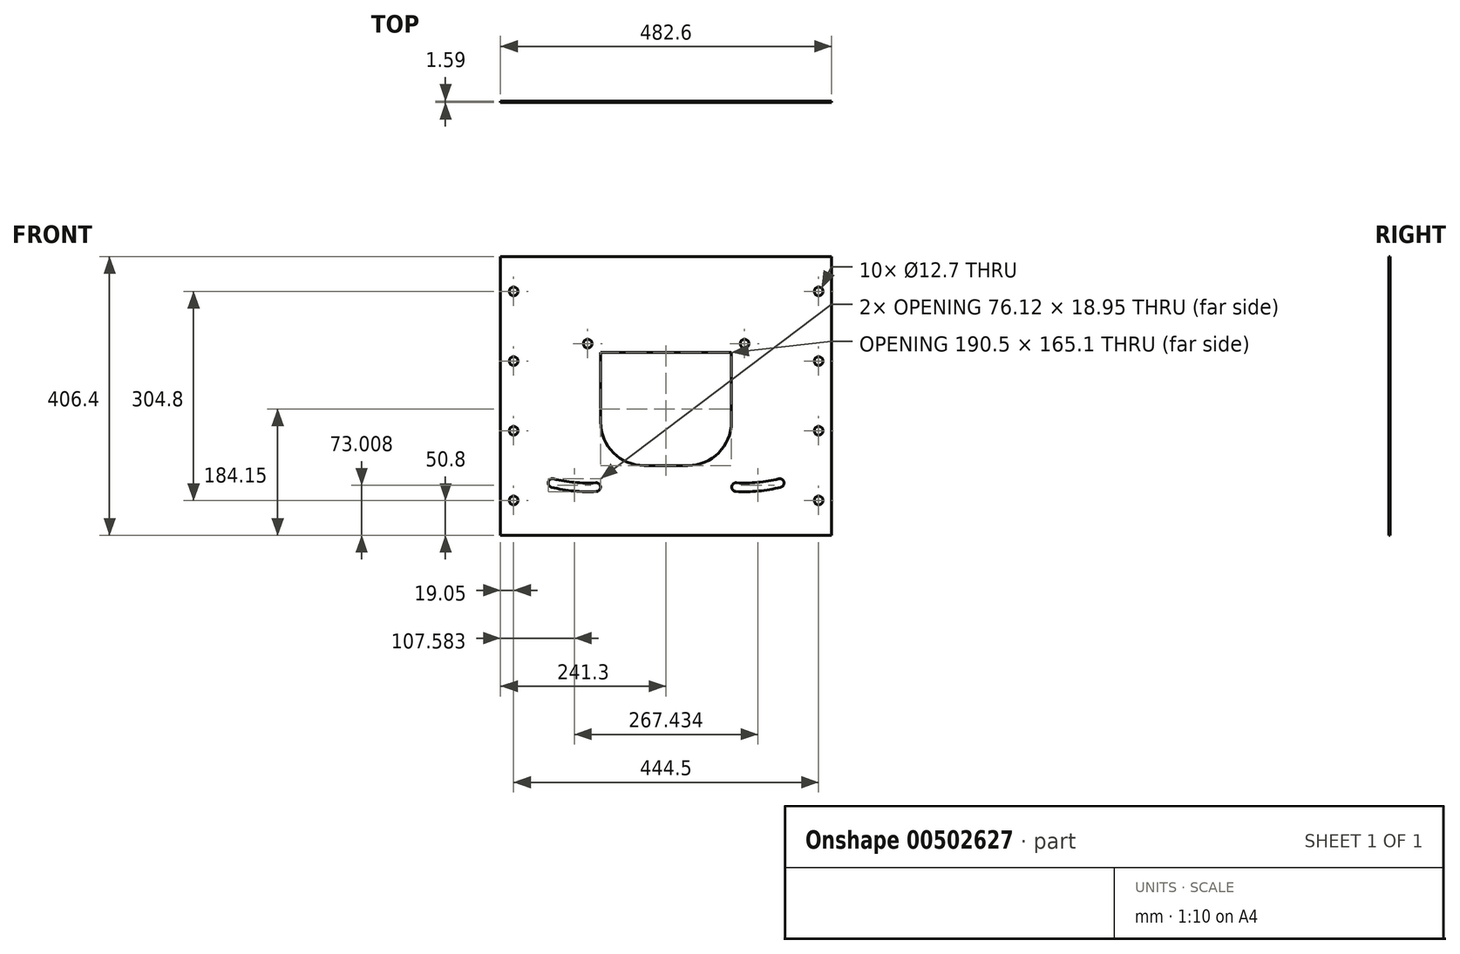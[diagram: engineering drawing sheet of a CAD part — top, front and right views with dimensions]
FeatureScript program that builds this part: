
annotation { "Feature Type Name" : "Feature", "Feature Type Description" : "" }
export const myFeature = defineFeature(function(context is Context, id is Id, definition is map)
    precondition{}
    {
        {
            var Q0;
            Q0=qCreatedBy(makeId("Front.planeOp"),FACE);
            var sketch = newSketch(context, id + "F0", { "sketchPlane" : qUnion([Q0])});
            skLineSegment(sketch, "E0.bottom", {"start": v(0, 0) * mm, "end": v(482.6, 0) * mm});
            skLineSegment(sketch, "E0.top", {"start": v(0, 304.8) * mm, "end": v(146.05, 304.8) * mm});
            skLineSegment(sketch, "E0.left", {"start": v(0, 0) * mm, "end": v(0, 304.8) * mm});
            skLineSegment(sketch, "E0.right", {"start": v(482.6, 0) * mm, "end": v(482.6, 304.8) * mm});
            skCircle(sketch, "E1", {"center": v(19.05, 254) * mm, "radius": 6.35 * mm});
            skCircle(sketch, "E2", {"center": v(19.05, 152.4) * mm, "radius": 6.35 * mm});
            skCircle(sketch, "E3", {"center": v(19.05, 50.8) * mm, "radius": 6.35 * mm});
            skCircle(sketch, "E4", {"center": v(463.55, 254) * mm, "radius": 6.35 * mm});
            skCircle(sketch, "E5", {"center": v(463.55, 152.4) * mm, "radius": 6.35 * mm});
            skCircle(sketch, "E6", {"center": v(463.55, 50.8) * mm, "radius": 6.35 * mm});
            skCircle(sketch, "E7", {"center": v(127, 279.4) * mm, "radius": 6.35 * mm});
            skCircle(sketch, "E8", {"center": v(355.6, 279.4) * mm, "radius": 6.35 * mm});
            skLineSegment(sketch, "E9.left", {"start": v(146.05, 266.7) * mm, "end": v(146.05, 165.1) * mm});
            skLineSegment(sketch, "E9.right", {"start": v(336.55, 266.7) * mm, "end": v(336.55, 165.1) * mm});
            skLineSegment(sketch, "E10.trimOffspring", {"start": v(336.55, 304.8) * mm, "end": v(482.6, 304.8) * mm});
            skLineSegment(sketch, "E11", {"start": v(209.55, 101.6) * mm, "end": v(273.05, 101.6) * mm});
            skPoint(sketch, "E12.visualSharp", {"position": v(146.05, 101.6) * mm});
            skArc(sketch, "E12.filletArc", {"start": v(146.05, 165.1) * mm, "mid": v(164.65, 120.2) * mm, "end": v(209.55, 101.6) * mm});
            skPoint(sketch, "E13.visualSharp", {"position": v(336.55, 101.6) * mm});
            skArc(sketch, "E13.filletArc", {"start": v(273.05, 101.6) * mm, "mid": v(317.95, 120.2) * mm, "end": v(336.55, 165.1) * mm});
            skLineSegment(sketch, "E14.bottom", {"start": v(146.05, 304.8) * mm, "end": v(349.25, 304.8) * mm});
            skLineSegment(sketch, "E14.top", {"start": v(146.05, 266.7) * mm, "end": v(336.55, 266.7) * mm});
            skArc(sketch, "E15", {"start": v(74.25, 70.04) * mm, "mid": v(106.73, 64.45) * mm, "end": v(139.68, 63.87) * mm});
            skArc(sketch, "E16.0", {"start": v(77.36, 82.36) * mm, "mid": v(107.92, 77.1) * mm, "end": v(138.93, 76.55) * mm});
            skPoint(sketch, "E17", {"position": v(77.36, 82.36) * mm});
            skPoint(sketch, "E18", {"position": v(138.93, 76.55) * mm});
            skPoint(sketch, "E19", {"position": v(139.68, 63.87) * mm});
            skArc(sketch, "E20", {"start": v(77.36, 82.36) * mm, "mid": v(69.65, 77.75) * mm, "end": v(74.25, 70.04) * mm});
            skArc(sketch, "E21", {"start": v(139.68, 63.87) * mm, "mid": v(145.64, 70.58) * mm, "end": v(138.93, 76.55) * mm});
            skLineSegment(sketch, "E22", {"start": v(241.3, 304.8) * mm, "end": v(241.3, 0) * mm, "construction": true});
            skArc(sketch, "E23.MirrorCS", {"start": v(408.35, 70.04) * mm, "mid": v(375.87, 64.45) * mm, "end": v(342.92, 63.87) * mm});
            skArc(sketch, "E24.MirrorCS", {"start": v(342.92, 63.87) * mm, "mid": v(336.96, 70.58) * mm, "end": v(343.67, 76.55) * mm});
            skArc(sketch, "E25.MirrorCS", {"start": v(405.24, 82.36) * mm, "mid": v(374.68, 77.1) * mm, "end": v(343.67, 76.55) * mm});
            skPoint(sketch, "E26.MirrorP", {"position": v(343.67, 76.55) * mm});
            skPoint(sketch, "E27.MirrorP", {"position": v(342.92, 63.87) * mm});
            skArc(sketch, "E28.MirrorCS", {"start": v(405.24, 82.36) * mm, "mid": v(412.95, 77.75) * mm, "end": v(408.35, 70.04) * mm});
            skPoint(sketch, "E29.MirrorP", {"position": v(405.24, 82.36) * mm});
            skLineSegment(sketch, "E30.bottom", {"start": v(0, 304.8) * mm, "end": v(482.6, 304.8) * mm});
            skSolve(sketch);
        }
        {
            var Q0;
            Q0=makeQuery(id+"F0.imprint","IMPRINT",FACE,{"disambiguationData":[TD([[makeQuery(id+"F0.imprint","IMPRINT",EDGE,{"derivedFrom":sQuery(id+"F0.wireOp",EDGE,"E0.bottom")}),1.0]])]});
            extrude(context, id + "F1", {"entities" : qUnion([Q0]), "depth" : 1.59 * mm});
        }
        {
            var Q0;
            Q0=makeQuery(id+"F1.opExtrude","CAP_FACE",FACE,{"disambiguationData":[OSD([sQuery(id+"F0.wireOp",EDGE,"E0.bottom"),sQuery(id+"F0.wireOp",EDGE,"E0.left"),sQuery(id+"F0.wireOp",EDGE,"E0.right"),sQuery(id+"F0.wireOp",EDGE,"E1"),sQuery(id+"F0.wireOp",EDGE,"E2"),sQuery(id+"F0.wireOp",EDGE,"E3"),sQuery(id+"F0.wireOp",EDGE,"E4"),sQuery(id+"F0.wireOp",EDGE,"E5"),sQuery(id+"F0.wireOp",EDGE,"E6"),sQuery(id+"F0.wireOp",EDGE,"E7"),sQuery(id+"F0.wireOp",EDGE,"E8"),sQuery(id+"F0.wireOp",EDGE,"E9.left"),sQuery(id+"F0.wireOp",EDGE,"E9.right"),sQuery(id+"F0.wireOp",EDGE,"E11"),sQuery(id+"F0.wireOp",EDGE,"E12.filletArc"),sQuery(id+"F0.wireOp",EDGE,"E13.filletArc"),sQuery(id+"F0.wireOp",EDGE,"E14.top"),sQuery(id+"F0.wireOp",EDGE,"E15"),sQuery(id+"F0.wireOp",EDGE,"E16.0"),sQuery(id+"F0.wireOp",EDGE,"E20"),sQuery(id+"F0.wireOp",EDGE,"E21"),sQuery(id+"F0.wireOp",EDGE,"E23.MirrorCS"),sQuery(id+"F0.wireOp",EDGE,"E24.MirrorCS"),sQuery(id+"F0.wireOp",EDGE,"E25.MirrorCS"),sQuery(id+"F0.wireOp",EDGE,"E28.MirrorCS"),sQuery(id+"F0.wireOp",EDGE,"E30.bottom")])],"isStart":false});
            var sketch = newSketch(context, id + "F2", { "sketchPlane" : qUnion([Q0])});
            skLineSegment(sketch, "E31.bottom", {"start": v(0, 304.8) * mm, "end": v(482.6, 304.8) * mm});
            skLineSegment(sketch, "E31.top", {"start": v(0, 406.4) * mm, "end": v(482.6, 406.4) * mm});
            skLineSegment(sketch, "E31.left", {"start": v(0, 304.8) * mm, "end": v(0, 406.4) * mm});
            skLineSegment(sketch, "E31.right", {"start": v(482.6, 304.8) * mm, "end": v(482.6, 406.4) * mm});
            skCircle(sketch, "E32", {"center": v(19.05, 355.6) * mm, "radius": 6.35 * mm});
            skCircle(sketch, "E33", {"center": v(463.55, 355.6) * mm, "radius": 6.35 * mm});
            skSolve(sketch);
        }
        {
            var Q0;
            Q0=makeQuery(id+"F2.imprint","IMPRINT",FACE,{"disambiguationData":[TD([[makeQuery(id+"F2.imprint","IMPRINT",EDGE,{"derivedFrom":sQuery(id+"F2.wireOp",EDGE,"E31.bottom")}),1.0]])]});
            extrude(context, id + "F3", {"entities" : qUnion([Q0]), "operationType" : NewBodyOperationType.ADD, "oppositeDirection" : true, "depth" : 1.59 * mm});
        }
    });
